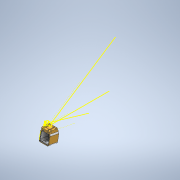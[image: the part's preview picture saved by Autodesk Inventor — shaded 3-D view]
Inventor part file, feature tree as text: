
AUTODESK INVENTOR PART (.ipt)
format: ipt  version: 2020 (Build 240168000, 168)  size: 337,920 bytes
history: native  units: mm
features: sketch x8, other x3, projected_geometry x2, extrude x1
ambient origin geometry x8: Origin, YZ Plane, XZ Plane, XY Plane, X Axis, Y Axis, Z Axis, Center Point
bodies: Solid1 (feature_tree)
feature tree (14):
  other  "V2 modular session with camera for cutout 45 deg.iam"
  other  "V2 session mount 45deg block.ipt:1"
  other  "45 deg predator nano mount.ipt:1"
  extrude  "Extrusion1"  Depth=10.0mm TaperAngle=0.0deg
  sketch  "Sketch6"
  sketch  "Sketch7"
  sketch  "Sketch1"  dims[d0=10.0mm d1=10.0mm d2=0.0mm]
  sketch  "Sketch1_1"
  sketch  "Sketch6_1"
  sketch  "Sketch11"
  sketch  "Sketch10_1"
  sketch  "Sketch10"
  projected_geometry  "Projected Loop1"
  projected_geometry  "Projected Loop2"
